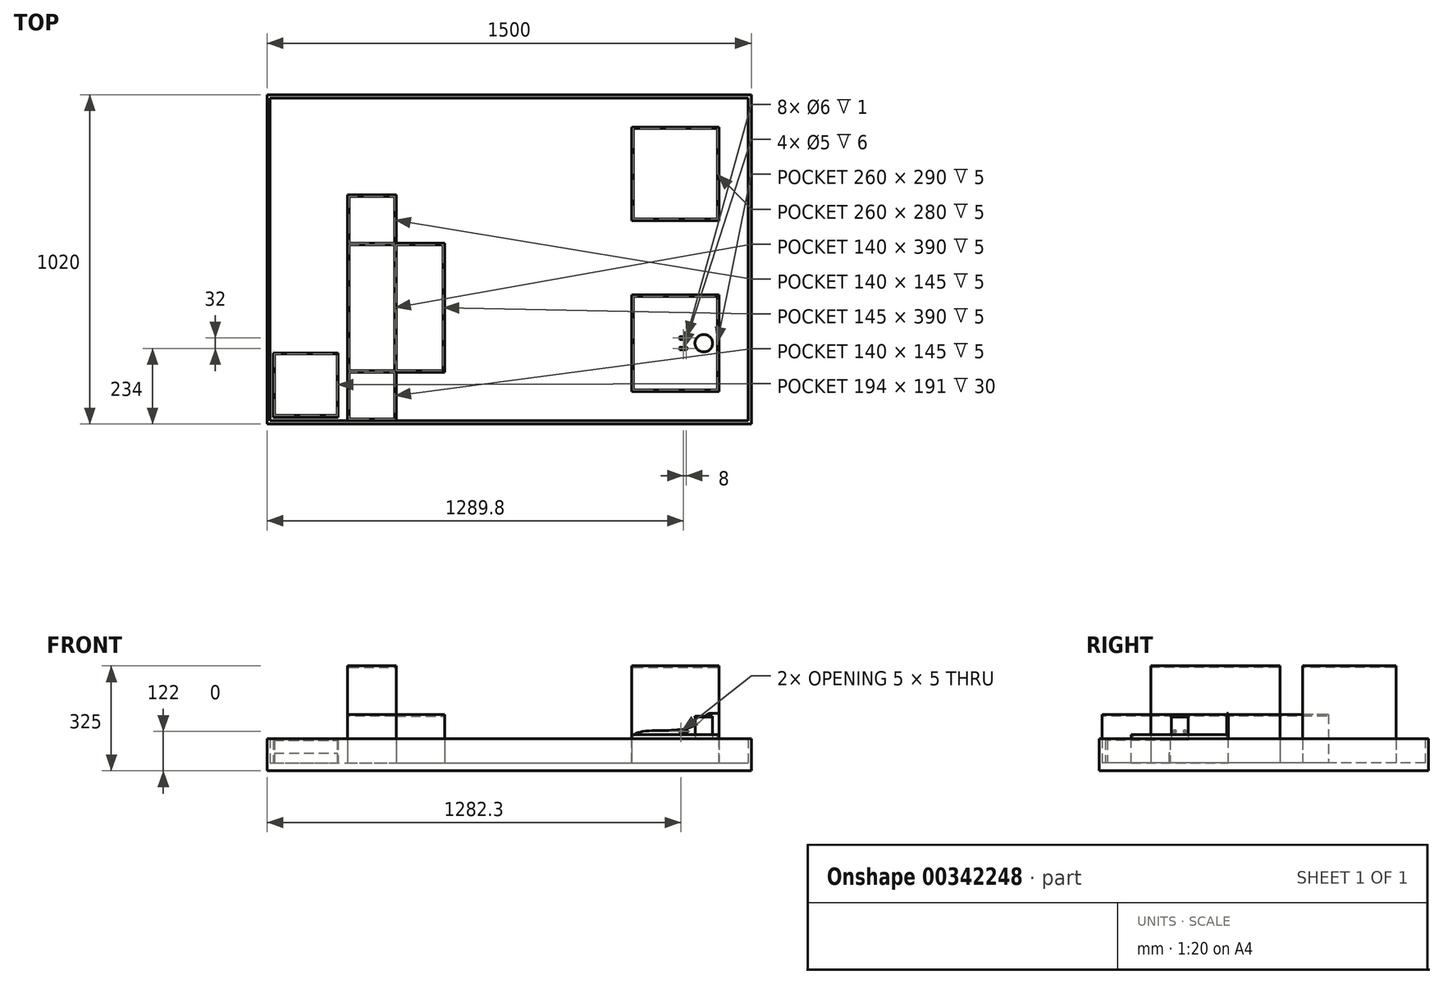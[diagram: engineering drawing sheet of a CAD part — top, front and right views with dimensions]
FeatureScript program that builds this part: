
annotation { "Feature Type Name" : "Feature", "Feature Type Description" : "" }
export const myFeature = defineFeature(function(context is Context, id is Id, definition is map)
    precondition{}
    {
        {
            var Q0;
            Q0=qCreatedBy(makeId("Top.planeOp"),FACE);
            var sketch = newSketch(context, id + "F0", { "sketchPlane" : qUnion([Q0])});
            skCircle(sketch, "E0", {"center": v(0, 0) * mm, "radius": 27.2 * mm});
            skSolve(sketch);
        }
        {
            var Q0;
            Q0=qSketchRegion(id+"F0",true);
            extrude(context, id + "F1", {"entities" : qUnion([Q0]), "depth" : 2.83 * mm});
        }
        {
            var Q0;
            Q0=makeQuery(id+"F1.opExtrude","CAP_FACE",FACE,{"disambiguationData":[OSD([sQuery(id+"F0.wireOp",EDGE,"E0")])],"isStart":false});
            var sketch = newSketch(context, id + "F2", { "sketchPlane" : qUnion([Q0])});
            skCircle(sketch, "E1", {"center": v(0, 0) * mm, "radius": 26.4 * mm});
            skSolve(sketch);
        }
        {
            var Q0;
            Q0=qSketchRegion(id+"F2",true);
            extrude(context, id + "F3", {"entities" : qUnion([Q0]), "operationType" : NewBodyOperationType.ADD, "depth" : 67.36 * mm});
        }
        {
            var Q0;
            Q0=makeQuery(id+"F3.opExtrude","CAP_FACE",FACE,{"disambiguationData":[OSD([sQuery(id+"F2.wireOp",EDGE,"E1")])],"isStart":false});
            var sketch = newSketch(context, id + "F4", { "sketchPlane" : qUnion([Q0])});
            skCircle(sketch, "E2", {"center": v(0, 0) * mm, "radius": 27.2 * mm});
            skSolve(sketch);
        }
        {
            var Q0;
            Q0=qSketchRegion(id+"F4",true);
            extrude(context, id + "F5", {"entities" : qUnion([Q0]), "operationType" : NewBodyOperationType.ADD, "depth" : 2.83 * mm});
        }
        {
            var Q0;
            Q0=makeQuery(id+"F5.opExtrude","CAP_FACE",FACE,{"disambiguationData":[OSD([sQuery(id+"F4.wireOp",EDGE,"E2")])],"isStart":false});
            var sketch = newSketch(context, id + "F6", { "sketchPlane" : qUnion([Q0])});
            skSolve(sketch);
        }
        {
            var Q0;
            Q0=qCreatedBy(makeId("Top.planeOp"),FACE);
            cPlane(context, id + "F7", {"entities" : qUnion([Q0]), "cplaneType" : CPlaneType.OFFSET, "offset" : 25 * mm, "width" : 150 * mm, "height" : 150 * mm});
        }
        {
            var Q0;
            Q0=makeQuery(id+"F6.imprint","IMPRINT",FACE,{"disambiguationData":[TD([[makeQuery(id+"F6.imprint","IMPRINT",EDGE,{"derivedFrom":makeQuery(id+"F5.opExtrude","CAP_EDGE",EDGE,{"disambiguationData":[OSD([sQuery(id+"F4.wireOp",EDGE,"E2")])],"isStart":false})}),1.0]])]});
            var sketch = newSketch(context, id + "F8", { "sketchPlane" : qUnion([Q0])});
            skSolve(sketch);
        }
        {
            var Q0;
            Q0=qCreatedBy(makeId("Top.planeOp"),FACE);
            var sketch = newSketch(context, id + "F9", { "sketchPlane" : qUnion([Q0])});
            skLineSegment(sketch, "E3.bottom", {"start": v(-222.8, -150) * mm, "end": v(47.2, -150) * mm});
            skLineSegment(sketch, "E3.top", {"start": v(-222.8, 150) * mm, "end": v(47.2, 150) * mm});
            skLineSegment(sketch, "E3.left", {"start": v(-222.8, -150) * mm, "end": v(-222.8, 150) * mm});
            skLineSegment(sketch, "E3.right", {"start": v(47.2, -150) * mm, "end": v(47.2, 150) * mm});
            skSolve(sketch);
        }
        {
            var Q0;
            Q0=qSketchRegion(id+"F9",true);
            extrude(context, id + "F10", {"entities" : qUnion([Q0]), "oppositeDirection" : true, "depth" : 72 * mm});
        }
        {
            var Q0;
            Q0=makeQuery(id+"F10.opExtrude","CAP_FACE",FACE,{"disambiguationData":[OSD([sQuery(id+"F9.wireOp",EDGE,"E3.bottom"),sQuery(id+"F9.wireOp",EDGE,"E3.top"),sQuery(id+"F9.wireOp",EDGE,"E3.left"),sQuery(id+"F9.wireOp",EDGE,"E3.right")])],"isStart":true});
            var sketch = newSketch(context, id + "F11", { "sketchPlane" : qUnion([Q0])});
            skLineSegment(sketch, "E4.bottom", {"start": v(-222.8, -150) * mm, "end": v(47.2, -150) * mm});
            skLineSegment(sketch, "E4.top", {"start": v(-222.8, -145) * mm, "end": v(42.2, -145) * mm});
            skLineSegment(sketch, "E4.left", {"start": v(-222.8, -150) * mm, "end": v(-222.8, -145) * mm});
            skLineSegment(sketch, "E5.bottom", {"start": v(47.2, 150) * mm, "end": v(42.2, 150) * mm});
            skLineSegment(sketch, "E5.left", {"start": v(47.2, 150) * mm, "end": v(47.2, -150) * mm});
            skLineSegment(sketch, "E5.right", {"start": v(42.2, 150) * mm, "end": v(42.2, -145) * mm});
            skSolve(sketch);
        }
        {
            var Q0;
            Q0=qSketchRegion(id+"F11",true);
            extrude(context, id + "F12", {"entities" : qUnion([Q0]), "operationType" : NewBodyOperationType.ADD, "depth" : 15 * mm});
        }
        {
            var Q0;
            Q0=makeQuery(id+"F12.boolean.opBoolean","MERGE",FACE,{"derivedFrom":[makeQuery(id+"F10.opExtrude","SWEPT_FACE",FACE,{"disambiguationData":[OSD([sQuery(id+"F9.wireOp",EDGE,"E3.top")])]}),makeQuery(id+"F12.opExtrude","SWEPT_FACE",FACE,{"disambiguationData":[OSD([sQuery(id+"F11.wireOp",EDGE,"E5.bottom")])]})]});
            var sketch = newSketch(context, id + "F13", { "sketchPlane" : qUnion([Q0])});
            skLineSegment(sketch, "E6", {"start": v(-47.2, 81.36) * mm, "end": v(-21.31, 81.36) * mm});
            skFitSpline(sketch, "E7", {"points": [v(-21.31, 81.36) * mm, v(15.24, 52.01) * mm, v(114.14, 28.17) * mm, v(222.8, 0) * mm], "startDerivative": vector(181.02, 0.3) * mm, "endDerivative": vector(-1.73, -239.85) * mm});
            skLineSegment(sketch, "E8", {"start": v(-47.2, 81.36) * mm, "end": v(-47.2, -72) * mm});
            skLineSegment(sketch, "E9", {"start": v(-47.2, -72) * mm, "end": v(222.8, -72) * mm});
            skLineSegment(sketch, "E10", {"start": v(222.8, -72) * mm, "end": v(222.8, 0) * mm});
            skSolve(sketch);
        }
        {
            var Q0;
            Q0=qSketchRegion(id+"F13",true);
            extrude(context, id + "F14", {"entities" : qUnion([Q0]), "operationType" : NewBodyOperationType.ADD, "oppositeDirection" : true, "depth" : 5 * mm});
        }
        {
            var Q0;
            Q0=makeQuery(id+"F10.opExtrude","CAP_FACE",FACE,{"disambiguationData":[OSD([sQuery(id+"F9.wireOp",EDGE,"E3.bottom"),sQuery(id+"F9.wireOp",EDGE,"E3.top"),sQuery(id+"F9.wireOp",EDGE,"E3.left"),sQuery(id+"F9.wireOp",EDGE,"E3.right")])],"isStart":true});
            var sketch = newSketch(context, id + "F15", { "sketchPlane" : qUnion([Q0])});
            skLineSegment(sketch, "E11.bottom", {"start": v(-222.8, 145) * mm, "end": v(-217.8, 145) * mm});
            skLineSegment(sketch, "E11.top", {"start": v(-222.8, -145) * mm, "end": v(-217.8, -145) * mm});
            skLineSegment(sketch, "E11.left", {"start": v(-222.8, 145) * mm, "end": v(-222.8, -145) * mm});
            skLineSegment(sketch, "E11.right", {"start": v(-217.8, 145) * mm, "end": v(-217.8, -145) * mm});
            skSolve(sketch);
        }
        {
            var Q0;
            Q0=qSketchRegion(id+"F15",true);
            extrude(context, id + "F16", {"entities" : qUnion([Q0]), "operationType" : NewBodyOperationType.ADD, "depth" : 5 * mm});
        }
        {
            var Q0;
            Q0=makeQuery(id+"F10.opExtrude","CAP_FACE",FACE,{"disambiguationData":[OSD([sQuery(id+"F9.wireOp",EDGE,"E3.bottom"),sQuery(id+"F9.wireOp",EDGE,"E3.top"),sQuery(id+"F9.wireOp",EDGE,"E3.left"),sQuery(id+"F9.wireOp",EDGE,"E3.right")])],"isStart":false});
            var sketch = newSketch(context, id + "F17", { "sketchPlane" : qUnion([Q0])});
            skLineSegment(sketch, "E12.bottom", {"start": v(147.2, 250) * mm, "end": v(-1352.8, 250) * mm});
            skLineSegment(sketch, "E12.top", {"start": v(147.2, -770) * mm, "end": v(-1352.8, -770) * mm});
            skLineSegment(sketch, "E12.left", {"start": v(147.2, 250) * mm, "end": v(147.2, -770) * mm});
            skLineSegment(sketch, "E12.right", {"start": v(-1352.8, 250) * mm, "end": v(-1352.8, -770) * mm});
            skSolve(sketch);
        }
        {
            var Q0;
            Q0=qSketchRegion(id+"F17",true);
            extrude(context, id + "F18", {"entities" : qUnion([Q0]), "operationType" : NewBodyOperationType.ADD, "depth" : 25 * mm});
        }
        {
            var Q0;
            Q0=makeQuery(id+"F18.opExtrude","CAP_FACE",FACE,{"disambiguationData":[OSD([sQuery(id+"F17.wireOp",EDGE,"E12.bottom"),sQuery(id+"F17.wireOp",EDGE,"E12.top"),sQuery(id+"F17.wireOp",EDGE,"E12.left"),sQuery(id+"F17.wireOp",EDGE,"E12.right")])],"isStart":true});
            var sketch = newSketch(context, id + "F19", { "sketchPlane" : qUnion([Q0])});
            skLineSegment(sketch, "E13.bottom", {"start": v(-222.8, 670) * mm, "end": v(47.2, 670) * mm});
            skLineSegment(sketch, "E13.top", {"start": v(-222.8, 380) * mm, "end": v(47.2, 380) * mm});
            skLineSegment(sketch, "E13.left", {"start": v(-222.8, 670) * mm, "end": v(-222.8, 380) * mm});
            skLineSegment(sketch, "E13.right", {"start": v(47.2, 670) * mm, "end": v(47.2, 380) * mm});
            skSolve(sketch);
        }
        {
            var Q0;
            Q0=qSketchRegion(id+"F19",true);
            extrude(context, id + "F20", {"entities" : qUnion([Q0]), "operationType" : NewBodyOperationType.ADD, "depth" : 300 * mm});
        }
        {
            var Q0;
            Q0=makeQuery(id+"F20.opExtrude","CAP_FACE",FACE,{"disambiguationData":[OSD([sQuery(id+"F19.wireOp",EDGE,"E13.bottom"),sQuery(id+"F19.wireOp",EDGE,"E13.top"),sQuery(id+"F19.wireOp",EDGE,"E13.left"),sQuery(id+"F19.wireOp",EDGE,"E13.right")])],"isStart":false});
            var sketch = newSketch(context, id + "F21", { "sketchPlane" : qUnion([Q0])});
            skLineSegment(sketch, "E14.bottom", {"start": v(-217.8, 665) * mm, "end": v(42.2, 665) * mm});
            skLineSegment(sketch, "E14.top", {"start": v(-217.8, 385) * mm, "end": v(42.2, 385) * mm});
            skLineSegment(sketch, "E14.left", {"start": v(-217.8, 665) * mm, "end": v(-217.8, 385) * mm});
            skLineSegment(sketch, "E14.right", {"start": v(42.2, 665) * mm, "end": v(42.2, 385) * mm});
            skSolve(sketch);
        }
        {
            var Q0;
            Q0=qSketchRegion(id+"F21",true);
            extrude(context, id + "F22", {"entities" : qUnion([Q0]), "operationType" : NewBodyOperationType.REMOVE, "oppositeDirection" : true, "depth" : 5 * mm});
        }
        {
            var Q0;
            Q0=makeQuery(id+"F18.opExtrude","CAP_FACE",FACE,{"disambiguationData":[OSD([sQuery(id+"F17.wireOp",EDGE,"E12.bottom"),sQuery(id+"F17.wireOp",EDGE,"E12.top"),sQuery(id+"F17.wireOp",EDGE,"E12.left"),sQuery(id+"F17.wireOp",EDGE,"E12.right")])],"isStart":true});
            var sketch = newSketch(context, id + "F23", { "sketchPlane" : qUnion([Q0])});
            skLineSegment(sketch, "E15.bottom", {"start": v(-1352.8, 770) * mm, "end": v(147.2, 770) * mm});
            skLineSegment(sketch, "E15.top", {"start": v(-1352.8, -250) * mm, "end": v(147.2, -250) * mm});
            skLineSegment(sketch, "E15.left", {"start": v(-1352.8, 770) * mm, "end": v(-1352.8, -250) * mm});
            skLineSegment(sketch, "E15.right", {"start": v(147.2, 770) * mm, "end": v(147.2, -250) * mm});
            skLineSegment(sketch, "E16.bottom", {"start": v(-1342.8, 760) * mm, "end": v(137.2, 760) * mm});
            skLineSegment(sketch, "E16.top", {"start": v(-1342.8, -240) * mm, "end": v(137.2, -240) * mm});
            skLineSegment(sketch, "E16.left", {"start": v(-1342.8, 760) * mm, "end": v(-1342.8, -240) * mm});
            skLineSegment(sketch, "E16.right", {"start": v(137.2, 760) * mm, "end": v(137.2, -240) * mm});
            skSolve(sketch);
        }
        {
            var Q0;
            Q0=qSketchRegion(id+"F23",true);
            extrude(context, id + "F24", {"entities" : qUnion([Q0]), "operationType" : NewBodyOperationType.ADD, "depth" : 75 * mm});
        }
        {
            var Q0;
            Q0=makeQuery(id+"F18.opExtrude","CAP_FACE",FACE,{"disambiguationData":[OSD([sQuery(id+"F17.wireOp",EDGE,"E12.bottom"),sQuery(id+"F17.wireOp",EDGE,"E12.top"),sQuery(id+"F17.wireOp",EDGE,"E12.left"),sQuery(id+"F17.wireOp",EDGE,"E12.right")])],"isStart":true});
            var sketch = newSketch(context, id + "F25", { "sketchPlane" : qUnion([Q0])});
            skLineSegment(sketch, "E17.bottom", {"start": v(-1102.8, 460) * mm, "end": v(-952.8, 460) * mm});
            skLineSegment(sketch, "E17.top", {"start": v(-1102.8, -240) * mm, "end": v(-952.8, -240) * mm});
            skLineSegment(sketch, "E17.left", {"start": v(-1102.8, 460) * mm, "end": v(-1102.8, -240) * mm});
            skLineSegment(sketch, "E17.right", {"start": v(-952.8, 460) * mm, "end": v(-952.8, 310) * mm});
            skLineSegment(sketch, "E18.bottom", {"start": v(-952.8, 310) * mm, "end": v(-802.8, 310) * mm});
            skLineSegment(sketch, "E18.top", {"start": v(-952.8, -90) * mm, "end": v(-802.8, -90) * mm});
            skLineSegment(sketch, "E18.right", {"start": v(-802.8, 310) * mm, "end": v(-802.8, -90) * mm});
            skLineSegment(sketch, "E19.trimOffspring", {"start": v(-952.8, -90) * mm, "end": v(-952.8, -240) * mm});
            skSolve(sketch);
        }
        {
            var Q0;
            Q0=qSketchRegion(id+"F25",true);
            extrude(context, id + "F26", {"entities" : qUnion([Q0]), "operationType" : NewBodyOperationType.ADD, "depth" : 150 * mm});
        }
        {
            var Q0;
            Q0=makeQuery(id+"F26.opExtrude","CAP_FACE",FACE,{"disambiguationData":[OSD([sQuery(id+"F25.wireOp",EDGE,"E17.bottom"),sQuery(id+"F25.wireOp",EDGE,"E17.top"),sQuery(id+"F25.wireOp",EDGE,"E17.left"),sQuery(id+"F25.wireOp",EDGE,"E17.right"),sQuery(id+"F25.wireOp",EDGE,"E18.bottom"),sQuery(id+"F25.wireOp",EDGE,"E18.top"),sQuery(id+"F25.wireOp",EDGE,"E18.right"),sQuery(id+"F25.wireOp",EDGE,"E19.trimOffspring")])],"isStart":false});
            var sketch = newSketch(context, id + "F27", { "sketchPlane" : qUnion([Q0])});
            skLineSegment(sketch, "E20.bottom", {"start": v(-952.8, 310) * mm, "end": v(-1102.8, 310) * mm});
            skLineSegment(sketch, "E20.top", {"start": v(-952.8, -90) * mm, "end": v(-1102.8, -90) * mm});
            skLineSegment(sketch, "E20.left", {"start": v(-952.8, 310) * mm, "end": v(-952.8, -90) * mm});
            skLineSegment(sketch, "E20.right", {"start": v(-1102.8, 310) * mm, "end": v(-1102.8, -90) * mm});
            skSolve(sketch);
        }
        {
            var Q0;
            Q0=qSketchRegion(id+"F27",true);
            extrude(context, id + "F28", {"entities" : qUnion([Q0]), "operationType" : NewBodyOperationType.ADD, "depth" : 150 * mm});
        }
        {
            var Q0;
            Q0=makeQuery(id+"F28.opExtrude","CAP_FACE",FACE,{"disambiguationData":[OSD([sQuery(id+"F27.wireOp",EDGE,"E20.bottom"),sQuery(id+"F27.wireOp",EDGE,"E20.top"),sQuery(id+"F27.wireOp",EDGE,"E20.left"),sQuery(id+"F27.wireOp",EDGE,"E20.right")])],"isStart":false});
            var sketch = newSketch(context, id + "F29", { "sketchPlane" : qUnion([Q0])});
            skLineSegment(sketch, "E21.bottom", {"start": v(-1097.8, 305) * mm, "end": v(-957.8, 305) * mm});
            skLineSegment(sketch, "E21.top", {"start": v(-1097.8, -85) * mm, "end": v(-957.8, -85) * mm});
            skLineSegment(sketch, "E21.left", {"start": v(-1097.8, 305) * mm, "end": v(-1097.8, -85) * mm});
            skLineSegment(sketch, "E21.right", {"start": v(-957.8, 305) * mm, "end": v(-957.8, -85) * mm});
            skSolve(sketch);
        }
        {
            var Q0;
            Q0=qSketchRegion(id+"F29",true);
            extrude(context, id + "F30", {"entities" : qUnion([Q0]), "operationType" : NewBodyOperationType.REMOVE, "oppositeDirection" : true, "depth" : 5 * mm});
        }
        {
            var Q0;
            {var subQ0=sQuery(id+"F25.wireOp",EDGE,"E17.left");var subQ1=sQuery(id+"F25.wireOp",EDGE,"E18.bottom");var subQ2=sQuery(id+"F25.wireOp",EDGE,"E17.right");var subQ3=sQuery(id+"F25.wireOp",EDGE,"E17.bottom");var subQ4=makeQuery(id+"F26.opExtrude","CAP_FACE",FACE,{"disambiguationData":[OSD([subQ3,sQuery(id+"F25.wireOp",EDGE,"E17.top"),subQ0,subQ2,subQ1,sQuery(id+"F25.wireOp",EDGE,"E18.top"),sQuery(id+"F25.wireOp",EDGE,"E18.right"),sQuery(id+"F25.wireOp",EDGE,"E19.trimOffspring")])],"isStart":false});Q0=makeQuery(id+"F28.boolean.opBoolean","SPLIT",FACE,{"disambiguationData":[TD([makeQuery(id+"F26.opExtrude","SWEPT_FACE",FACE,{"disambiguationData":[OSD([subQ3])]})])],"derivedFrom":subQ4});}
            var sketch = newSketch(context, id + "F31", { "sketchPlane" : qUnion([Q0])});
            skLineSegment(sketch, "E22.bottom", {"start": v(-1097.8, 455) * mm, "end": v(-957.8, 455) * mm});
            skLineSegment(sketch, "E22.top", {"start": v(-1097.8, 310) * mm, "end": v(-957.8, 310) * mm});
            skLineSegment(sketch, "E22.left", {"start": v(-1097.8, 455) * mm, "end": v(-1097.8, 310) * mm});
            skLineSegment(sketch, "E22.right", {"start": v(-957.8, 455) * mm, "end": v(-957.8, 310) * mm});
            skLineSegment(sketch, "E23.bottom", {"start": v(-952.8, 305) * mm, "end": v(-807.8, 305) * mm});
            skLineSegment(sketch, "E23.top", {"start": v(-952.8, -85) * mm, "end": v(-807.8, -85) * mm});
            skLineSegment(sketch, "E23.left", {"start": v(-952.8, 305) * mm, "end": v(-952.8, -85) * mm});
            skLineSegment(sketch, "E23.right", {"start": v(-807.8, 305) * mm, "end": v(-807.8, -85) * mm});
            skLineSegment(sketch, "E24.bottom", {"start": v(-1097.8, -90) * mm, "end": v(-957.8, -90) * mm});
            skLineSegment(sketch, "E24.top", {"start": v(-1097.8, -235) * mm, "end": v(-957.8, -235) * mm});
            skLineSegment(sketch, "E24.left", {"start": v(-1097.8, -90) * mm, "end": v(-1097.8, -235) * mm});
            skLineSegment(sketch, "E24.right", {"start": v(-957.8, -90) * mm, "end": v(-957.8, -235) * mm});
            skSolve(sketch);
        }
        {
            var Q0;
            Q0=qSketchRegion(id+"F31",true);
            extrude(context, id + "F32", {"entities" : qUnion([Q0]), "operationType" : NewBodyOperationType.REMOVE, "oppositeDirection" : true, "depth" : 5 * mm});
        }
        {
            var Q0;
            Q0=qCreatedBy(id+"F7.planeOp",FACE);
            var sketch = newSketch(context, id + "F33", { "sketchPlane" : qUnion([Q0])});
            skLineSegment(sketch, "E25", {"start": v(0, 0) * mm, "end": v(-90, 0) * mm, "construction": true});
            skLineSegment(sketch, "E26.bottom", {"start": v(-74.5, -12) * mm, "end": v(-55, -12) * mm});
            skLineSegment(sketch, "E26.top", {"start": v(-74.5, -20) * mm, "end": v(-55, -20) * mm});
            skLineSegment(sketch, "E26.left", {"start": v(-74.5, -12) * mm, "end": v(-74.5, -13) * mm});
            skPoint(sketch, "E27.visualSharp", {"position": v(-51, -12) * mm});
            skPoint(sketch, "E28.visualSharp", {"position": v(-51, -20) * mm});
            skCircle(sketch, "E29", {"center": v(-55, -16) * mm, "radius": 3 * mm});
            skLineSegment(sketch, "E30", {"start": v(-59, -3.98) * mm, "end": v(-59, -18.08) * mm, "construction": true});
            skCircle(sketch, "E31.MirrorC", {"center": v(-63, -16) * mm, "radius": 3 * mm});
            skLineSegment(sketch, "E32.bottom", {"start": v(-74.5, -13) * mm, "end": v(-65.65, -13) * mm});
            skLineSegment(sketch, "E32.top", {"start": v(-74.5, -19) * mm, "end": v(-65.65, -19) * mm});
            skArc(sketch, "E33", {"start": v(-65.65, -13) * mm, "mid": v(-67, -16) * mm, "end": v(-65.65, -19) * mm});
            skLineSegment(sketch, "E34.trimOffspring", {"start": v(-74.5, -19) * mm, "end": v(-74.5, -20) * mm});
            skArc(sketch, "E35.trimOffspring", {"start": v(-55, -20) * mm, "mid": v(-51, -16) * mm, "end": v(-55, -12) * mm});
            skLineSegment(sketch, "E36.MirrorCS", {"start": v(-74.5, 12) * mm, "end": v(-74.5, 13) * mm});
            skLineSegment(sketch, "E37.MirrorCS", {"start": v(-74.5, 19) * mm, "end": v(-74.5, 20) * mm});
            skPoint(sketch, "E38.MirrorP", {"position": v(-51, 12) * mm});
            skLineSegment(sketch, "E39.MirrorCS", {"start": v(-74.5, 12) * mm, "end": v(-55, 12) * mm});
            skPoint(sketch, "E40.MirrorP", {"position": v(-51, 20) * mm});
            skArc(sketch, "E41.MirrorCS", {"start": v(-65.65, 13) * mm, "mid": v(-67, 16) * mm, "end": v(-65.65, 19) * mm});
            skArc(sketch, "E42.MirrorCS", {"start": v(-55, 20) * mm, "mid": v(-51, 16) * mm, "end": v(-55, 12) * mm});
            skLineSegment(sketch, "E43.MirrorCS", {"start": v(-74.5, 20) * mm, "end": v(-55, 20) * mm});
            skCircle(sketch, "E44.MirrorC", {"center": v(-55, 16) * mm, "radius": 3 * mm});
            skCircle(sketch, "E45.MirrorC", {"center": v(-63, 16) * mm, "radius": 3 * mm});
            skLineSegment(sketch, "E46.MirrorCS", {"start": v(-74.5, 19) * mm, "end": v(-65.65, 19) * mm});
            skLineSegment(sketch, "E47.MirrorCS", {"start": v(-74.5, 13) * mm, "end": v(-65.65, 13) * mm});
            skSolve(sketch);
        }
        {
            var Q0;
            Q0=qSketchRegion(id+"F33",true);
            var Q1;
            Q1=qSketchRegion(id+"F36",true);
            extrude(context, id + "F34", {"entities" : qUnion([Q0, Q1]), "endBound" : BoundingType.SYMMETRIC, "depth" : 8 * mm});
        }
        {
            var Q0;
            Q0=makeQuery(id+"F34.opExtrude","CAP_EDGE",EDGE,{"disambiguationData":[OSD([sQuery(id+"F33.wireOp",EDGE,"E34.trimOffspring")])],"isStart":false});
            var Q1;
            Q1=makeQuery(id+"F34.opExtrude","CAP_EDGE",EDGE,{"disambiguationData":[OSD([sQuery(id+"F33.wireOp",EDGE,"E26.left")])],"isStart":false});
            var Q2;
            Q2=makeQuery(id+"F34.opExtrude","CAP_EDGE",EDGE,{"disambiguationData":[OSD([sQuery(id+"F33.wireOp",EDGE,"E34.trimOffspring")])],"isStart":true});
            var Q3;
            Q3=makeQuery(id+"F34.opExtrude","CAP_EDGE",EDGE,{"disambiguationData":[OSD([sQuery(id+"F33.wireOp",EDGE,"E26.left")])],"isStart":true});
            var Q4;
            Q4=makeQuery(id+"F34.opExtrude","CAP_EDGE",EDGE,{"disambiguationData":[OSD([sQuery(id+"F33.wireOp",EDGE,"E36.MirrorCS")])],"isStart":false});
            var Q5;
            Q5=makeQuery(id+"F34.opExtrude","CAP_EDGE",EDGE,{"disambiguationData":[OSD([sQuery(id+"F33.wireOp",EDGE,"E37.MirrorCS")])],"isStart":false});
            var Q6;
            Q6=makeQuery(id+"F34.opExtrude","CAP_EDGE",EDGE,{"disambiguationData":[OSD([sQuery(id+"F33.wireOp",EDGE,"E37.MirrorCS")])],"isStart":true});
            var Q7;
            Q7=makeQuery(id+"F34.opExtrude","CAP_EDGE",EDGE,{"disambiguationData":[OSD([sQuery(id+"F33.wireOp",EDGE,"E36.MirrorCS")])],"isStart":true});
            fillet(context, id + "F35", {"entities" : qUnion([Q0, Q1, Q2, Q3, Q4, Q5, Q6, Q7]), "radius" : 4 * mm, "tangentPropagation" : true, "allowEdgeOverflow" : false});
        }
        {
            var Q0;
            Q0=makeQuery(id+"F34.opExtrude","SWEPT_FACE",FACE,{"disambiguationData":[OSD([sQuery(id+"F33.wireOp",EDGE,"E26.top")])]});
            var sketch = newSketch(context, id + "F36", { "sketchPlane" : qUnion([Q0])});
            skCircle(sketch, "E48", {"center": v(-70.5, 25) * mm, "radius": 3 * mm});
            skSolve(sketch);
        }
        {
            var Q0;
            Q0=qSketchRegion(id+"F36",true);
            var Q1;
            Q1=makeQuery(id+"F34.opExtrude","SWEPT_FACE",FACE,{"disambiguationData":[OSD([sQuery(id+"F33.wireOp",EDGE,"E26.bottom")])]});
            extrude(context, id + "F37", {"entities" : qUnion([Q0]), "operationType" : NewBodyOperationType.ADD, "endBound" : BoundingType.UP_TO_SURFACE, "oppositeDirection" : true, "endBoundEntityFace" : qUnion([Q1]), "depth" : 25 * mm});
        }
        {
            var Q0;
            Q0=makeQuery(id+"F34.opExtrude","SWEPT_FACE",FACE,{"disambiguationData":[OSD([sQuery(id+"F33.wireOp",EDGE,"E43.MirrorCS")])]});
            var sketch = newSketch(context, id + "F38", { "sketchPlane" : qUnion([Q0])});
            skCircle(sketch, "E49", {"center": v(70.5, 25) * mm, "radius": 3 * mm});
            skSolve(sketch);
        }
        {
            var Q0;
            Q0=qSketchRegion(id+"F38",true);
            var Q1;
            Q1=makeQuery(id+"F34.opExtrude","SWEPT_FACE",FACE,{"disambiguationData":[OSD([sQuery(id+"F33.wireOp",EDGE,"E39.MirrorCS")])]});
            extrude(context, id + "F39", {"entities" : qUnion([Q0]), "operationType" : NewBodyOperationType.ADD, "endBound" : BoundingType.UP_TO_SURFACE, "oppositeDirection" : true, "endBoundEntityFace" : qUnion([Q1]), "depth" : 25 * mm});
        }
        {
            var Q0;
            Q0=qCreatedBy(id+"F7.planeOp",FACE);
            var sketch = newSketch(context, id + "F40", { "sketchPlane" : qUnion([Q0])});
            skCircle(sketch, "E50", {"center": v(-55, 16) * mm, "radius": 3 * mm});
            skCircle(sketch, "E51", {"center": v(-63, 16) * mm, "radius": 2.5 * mm});
            skCircle(sketch, "E52", {"center": v(-63, 16) * mm, "radius": 3 * mm});
            skCircle(sketch, "E53", {"center": v(-55, 16) * mm, "radius": 2.5 * mm});
            skSolve(sketch);
        }
        {
            var Q0;
            Q0=qSketchRegion(id+"F40",true);
            extrude(context, id + "F41", {"entities" : qUnion([Q0]), "operationType" : NewBodyOperationType.ADD, "endBound" : BoundingType.SYMMETRIC, "depth" : 6 * mm});
        }
        {
            var Q0;
            Q0=qCreatedBy(id+"F7.planeOp",FACE);
            var sketch = newSketch(context, id + "F42", { "sketchPlane" : qUnion([Q0])});
            skCircle(sketch, "E54", {"center": v(-63, -16) * mm, "radius": 2.5 * mm});
            skCircle(sketch, "E55", {"center": v(-63, -16) * mm, "radius": 3 * mm});
            skCircle(sketch, "E56", {"center": v(-55, -16) * mm, "radius": 2.5 * mm});
            skCircle(sketch, "E57", {"center": v(-55, -16) * mm, "radius": 3 * mm});
            skSolve(sketch);
        }
        {
            var Q0;
            Q0=qSketchRegion(id+"F42",true);
            extrude(context, id + "F43", {"entities" : qUnion([Q0]), "operationType" : NewBodyOperationType.ADD, "endBound" : BoundingType.SYMMETRIC, "depth" : 6 * mm});
        }
        {
            var Q0;
            Q0=makeQuery(id+"F34.opExtrude","SWEPT_FACE",FACE,{"disambiguationData":[OSD([sQuery(id+"F33.wireOp",EDGE,"E43.MirrorCS")])]});
            var sketch = newSketch(context, id + "F44", { "sketchPlane" : qUnion([Q0])});
            skArc(sketch, "E58", {"start": v(71.5, 27.3) * mm, "mid": v(70.5, 27.5) * mm, "end": v(69.5, 27.3) * mm});
            skLineSegment(sketch, "E59.bottom", {"start": v(68.2, 26) * mm, "end": v(69.5, 26) * mm});
            skLineSegment(sketch, "E59.top", {"start": v(68.2, 24) * mm, "end": v(69.5, 24) * mm});
            skLineSegment(sketch, "E60.left", {"start": v(71.5, 27.3) * mm, "end": v(71.5, 26) * mm});
            skLineSegment(sketch, "E60.right", {"start": v(69.5, 27.3) * mm, "end": v(69.5, 26) * mm});
            skPoint(sketch, "E61.orphan", {"position": v(69.5, 27.8) * mm});
            skPoint(sketch, "E62.orphan", {"position": v(71.5, 27.8) * mm});
            skArc(sketch, "E63.trimOffspring", {"start": v(68.2, 26) * mm, "mid": v(68, 25) * mm, "end": v(68.2, 24) * mm});
            skPoint(sketch, "E59.left.start.orphan", {"position": v(67.32, 26) * mm});
            skPoint(sketch, "E64.orphan", {"position": v(67.32, 24) * mm});
            skArc(sketch, "E65.trimOffspring", {"start": v(69.5, 22.7) * mm, "mid": v(70.5, 22.5) * mm, "end": v(71.5, 22.7) * mm});
            skLineSegment(sketch, "E66.trimOffspring", {"start": v(69.5, 24) * mm, "end": v(69.5, 22.7) * mm});
            skLineSegment(sketch, "E67.trimOffspring", {"start": v(71.5, 26) * mm, "end": v(72.8, 26) * mm});
            skLineSegment(sketch, "E68.trimOffspring", {"start": v(71.5, 24) * mm, "end": v(71.5, 22.7) * mm});
            skLineSegment(sketch, "E69.trimOffspring", {"start": v(71.5, 24) * mm, "end": v(72.8, 24) * mm});
            skPoint(sketch, "E60.top.end.orphan", {"position": v(69.5, 22.2) * mm});
            skPoint(sketch, "E70.orphan", {"position": v(71.5, 22.2) * mm});
            skPoint(sketch, "E59.right.end.orphan", {"position": v(73.68, 24) * mm});
            skPoint(sketch, "E71.orphan", {"position": v(73.68, 26) * mm});
            skArc(sketch, "E72.trimOffspring", {"start": v(72.8, 24) * mm, "mid": v(73, 25) * mm, "end": v(72.8, 26) * mm});
            skSolve(sketch);
        }
        {
            var Q0;
            Q0=qSketchRegion(id+"F44",true);
            extrude(context, id + "F45", {"entities" : qUnion([Q0]), "operationType" : NewBodyOperationType.REMOVE, "endBound" : BoundingType.THROUGH_ALL, "oppositeDirection" : true, "depth" : 25 * mm});
        }
        {
            var Q0;
            Q0=makeQuery(id+"F18.opExtrude","CAP_FACE",FACE,{"disambiguationData":[OSD([sQuery(id+"F17.wireOp",EDGE,"E12.bottom"),sQuery(id+"F17.wireOp",EDGE,"E12.top"),sQuery(id+"F17.wireOp",EDGE,"E12.left"),sQuery(id+"F17.wireOp",EDGE,"E12.right")])],"isStart":true});
            var sketch = newSketch(context, id + "F46", { "sketchPlane" : qUnion([Q0])});
            skLineSegment(sketch, "E73.bottom", {"start": v(-1332.8, -30) * mm, "end": v(-1132.8, -30) * mm});
            skLineSegment(sketch, "E73.top", {"start": v(-1332.8, -230) * mm, "end": v(-1132.8, -230) * mm});
            skLineSegment(sketch, "E73.left", {"start": v(-1332.8, -30) * mm, "end": v(-1332.8, -230) * mm});
            skLineSegment(sketch, "E73.right", {"start": v(-1132.8, -30) * mm, "end": v(-1132.8, -230) * mm});
            skLineSegment(sketch, "E74.bottom", {"start": v(-1329.8, -33) * mm, "end": v(-1135.8, -33) * mm});
            skLineSegment(sketch, "E74.top", {"start": v(-1329.8, -224) * mm, "end": v(-1135.8, -224) * mm});
            skLineSegment(sketch, "E74.left", {"start": v(-1329.8, -33) * mm, "end": v(-1329.8, -224) * mm});
            skLineSegment(sketch, "E74.right", {"start": v(-1135.8, -33) * mm, "end": v(-1135.8, -224) * mm});
            skSolve(sketch);
        }
        {
            var Q0;
            Q0=qSketchRegion(id+"F46",true);
            extrude(context, id + "F47", {"entities" : qUnion([Q0]), "operationType" : NewBodyOperationType.ADD, "depth" : 30 * mm});
        }
        {
            var Q0;
            Q0=makeQuery(id+"F47.opExtrude","CAP_FACE",FACE,{"disambiguationData":[OSD([sQuery(id+"F46.wireOp",EDGE,"E73.bottom"),sQuery(id+"F46.wireOp",EDGE,"E73.top"),sQuery(id+"F46.wireOp",EDGE,"E73.left"),sQuery(id+"F46.wireOp",EDGE,"E73.right"),sQuery(id+"F46.wireOp",EDGE,"E74.bottom"),sQuery(id+"F46.wireOp",EDGE,"E74.top"),sQuery(id+"F46.wireOp",EDGE,"E74.left"),sQuery(id+"F46.wireOp",EDGE,"E74.right")])],"isStart":false});
            var sketch = newSketch(context, id + "F48", { "sketchPlane" : qUnion([Q0])});
            skLineSegment(sketch, "E75.bottom", {"start": v(-1332.8, -30) * mm, "end": v(-1329.8, -30) * mm});
            skLineSegment(sketch, "E75.top", {"start": v(-1332.8, -230) * mm, "end": v(-1329.8, -230) * mm});
            skLineSegment(sketch, "E75.left", {"start": v(-1332.8, -30) * mm, "end": v(-1332.8, -230) * mm});
            skLineSegment(sketch, "E75.right", {"start": v(-1329.8, -30) * mm, "end": v(-1329.8, -224) * mm});
            skLineSegment(sketch, "E76.bottom", {"start": v(-1329.8, -230) * mm, "end": v(-1135.8, -230) * mm});
            skLineSegment(sketch, "E76.top", {"start": v(-1329.8, -224) * mm, "end": v(-1135.8, -224) * mm});
            skLineSegment(sketch, "E77.bottom", {"start": v(-1135.8, -230) * mm, "end": v(-1132.8, -230) * mm});
            skLineSegment(sketch, "E77.top", {"start": v(-1135.8, -30) * mm, "end": v(-1132.8, -30) * mm});
            skLineSegment(sketch, "E77.left", {"start": v(-1135.8, -224) * mm, "end": v(-1135.8, -30) * mm});
            skLineSegment(sketch, "E77.right", {"start": v(-1132.8, -230) * mm, "end": v(-1132.8, -30) * mm});
            skSolve(sketch);
        }
        {
            var Q0;
            Q0=qSketchRegion(id+"F48",true);
            extrude(context, id + "F49", {"entities" : qUnion([Q0]), "operationType" : NewBodyOperationType.ADD, "depth" : 40 * mm});
        }
        {
            var Q0;
            Q0=makeQuery(id+"F34.opExtrude","CAP_FACE",FACE,{"disambiguationData":[OSD([sQuery(id+"F33.wireOp",EDGE,"E36.MirrorCS"),sQuery(id+"F33.wireOp",EDGE,"E37.MirrorCS"),sQuery(id+"F33.wireOp",EDGE,"E39.MirrorCS"),sQuery(id+"F33.wireOp",EDGE,"E41.MirrorCS"),sQuery(id+"F33.wireOp",EDGE,"E42.MirrorCS"),sQuery(id+"F33.wireOp",EDGE,"E43.MirrorCS"),sQuery(id+"F33.wireOp",EDGE,"E44.MirrorC"),sQuery(id+"F33.wireOp",EDGE,"E45.MirrorC"),sQuery(id+"F33.wireOp",EDGE,"E46.MirrorCS"),sQuery(id+"F33.wireOp",EDGE,"E47.MirrorCS")])],"isStart":false});
            var sketch = newSketch(context, id + "F50", { "sketchPlane" : qUnion([Q0])});
            skLineSegment(sketch, "E78.bottom", {"start": v(-78.97, 27.08) * mm, "end": v(-0.62, 27.08) * mm});
            skLineSegment(sketch, "E78.top", {"start": v(-78.97, -29.9) * mm, "end": v(-0.62, -29.9) * mm});
            skLineSegment(sketch, "E78.left", {"start": v(-78.97, 27.08) * mm, "end": v(-78.97, 12) * mm});
            skLineSegment(sketch, "E78.right", {"start": v(-0.62, 27.08) * mm, "end": v(-0.62, -29.9) * mm});
            skLineSegment(sketch, "E79.bottom", {"start": v(-78.97, 12) * mm, "end": v(-44.82, 12) * mm});
            skLineSegment(sketch, "E79.top", {"start": v(-78.97, -8.24) * mm, "end": v(-44.82, -8.24) * mm});
            skLineSegment(sketch, "E79.right", {"start": v(-44.82, 12) * mm, "end": v(-44.82, -8.24) * mm});
            skLineSegment(sketch, "E80.trimOffspring", {"start": v(-78.97, -8.24) * mm, "end": v(-78.97, -29.9) * mm});
            skCircle(sketch, "E81", {"center": v(-63, 16) * mm, "radius": 2.5 * mm});
            skSolve(sketch);
        }
        {
            var Q0;
            Q0=qSketchRegion(id+"F50",true);
            extrude(context, id + "F51", {"entities" : qUnion([Q0]), "depth" : 8 * mm});
        }
        {
            var Q0;
            Q0=makeQuery(id+"F51.opExtrude","SWEPT_BODY",BODY,{"disambiguationData":[OSD([sQuery(id+"F50.wireOp",EDGE,"E78.bottom"),sQuery(id+"F50.wireOp",EDGE,"E78.top"),sQuery(id+"F50.wireOp",EDGE,"E78.left"),sQuery(id+"F50.wireOp",EDGE,"E78.right"),sQuery(id+"F50.wireOp",EDGE,"E79.bottom"),sQuery(id+"F50.wireOp",EDGE,"E79.top"),sQuery(id+"F50.wireOp",EDGE,"E79.right"),sQuery(id+"F50.wireOp",EDGE,"E80.trimOffspring"),sQuery(id+"F50.wireOp",EDGE,"E81")])]});
            deleteBodies(context, id + "F52", {"entities" : qUnion([Q0])});
        }
    });
